# Revit family: Sanitary_Bath-And-Spas_Sanindusa_Vertice_Bathtub-1800x800
name_source: partatom
category: Plumbing Fixtures
revit_build: Autodesk Revit 2018 (Build: 20170223_1515(x64)
units: mm (PartAtom-declared; Revit-internal decimal feet)

## family parameters
Cut with Voids When Loaded = No
Host = Face
Part Type = Normal
Room Calculation Point = No
Round Connector Dimension = Use Diameter
Shared = No

## types (1)
- Sanitary_Bath-And-Spas_Sanindusa_Vertice_Bathtub-1800x800
    AssetType = Fixed
    BarCode = 5604815436518
    Color = white
    Constituents = ref.490-50 automatic pop up waste for bathtub(not included); ref.811-70 fix kit feets for bathtub(not included); ref.800302-80 Panel(not included); ref. 805101-180 vertice panel(not included); 805606-Headrest for bathtub vértice(not included).
    Default Elevation = 1219 mm
    Description = Sanitary appliance for immersion of the human body or parts of it (BS6100)
    DrainSize = 52 mm
    Element Type = BATH: Sanitary appliance for immersion of the human body or parts of it (BS6100)
    Features = Bathtub for residential or hotel solution. Range with various sizes available.
    Finish = gloss
    Installation Instructions = https://www.tec.sanindusa.pt
    Manufacturer = Sanindusa
    ManufacturerName = Sanindusa
    ManufacturerURL = www.tec.sanindusa.pt
    Material = 3.2 mm acrylic sheet reinforced with polyester resin, fiberglass and 16 mm wood agglomerate on the bottom
    Model = 8061000000
    ModelNumber = 8061000000
    ModelReference = Vertice
    Name = Bathtub vertice 180x80
    NominalHeight = 405 mm
    NominalLength = 1800 mm  [stored 5.90551 ft]
    NominalWidth = 800 mm  [stored 2.62467 ft]
    Pre-defined type (IFC) = BATH
    ProductInformation = https://www.tec.sanindusa.pt
    ProductionYear = 2019
    Shape = Rectangular
    Size = 1800x800
    SpilloverLevel = 215 (L)
    Type (IFC) = IfcSanitaryTerminalType
    URL = www.tec.sanindusa.pt
    Uniclass2015Code = Ss_​40_​15_​75_​05
    Uniclass2015Title = Bath systems
    Uniclass2015Version = Systems v1.9
    Version = 1
    WarrantyDescription = https://www.tec.sanindusa.pt
    WarrantyDurationParts = 5
    Waste Connection = Yes
    Weight = 0.00 kg

note: [stored X ft] marks values corroborated as IEEE doubles in the binary element streams (Revit-internal decimal feet)

## geometry (parser evidence)
native form markers: Extrusion x1, Sweep x6
no freeform markers — native parametric forms only
